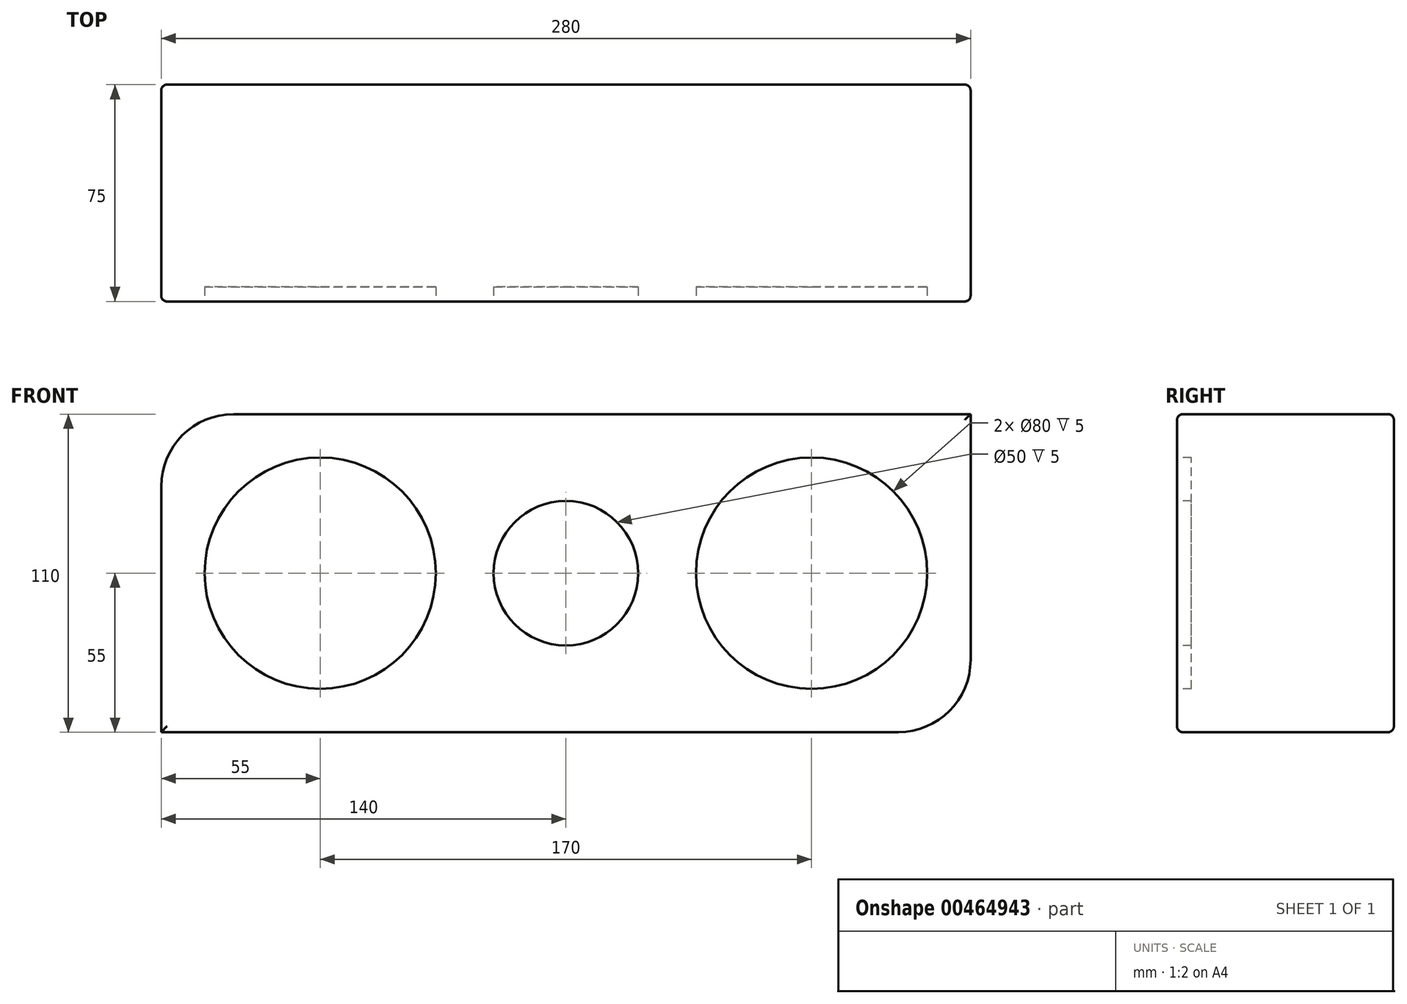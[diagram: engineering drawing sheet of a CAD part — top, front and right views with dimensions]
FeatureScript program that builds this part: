
annotation { "Feature Type Name" : "Feature", "Feature Type Description" : "" }
export const myFeature = defineFeature(function(context is Context, id is Id, definition is map)
    precondition{}
    {
        {
            var Q0;
            Q0=qCreatedBy(makeId("Front.planeOp"),FACE);
            var sketch = newSketch(context, id + "F0", { "sketchPlane" : qUnion([Q0])});
            skLineSegment(sketch, "E0.bottom", {"start": v(-140, -55) * mm, "end": v(115, -55) * mm});
            skLineSegment(sketch, "E0.top", {"start": v(-115, 55) * mm, "end": v(140, 55) * mm});
            skLineSegment(sketch, "E0.left", {"start": v(-140, -55) * mm, "end": v(-140, 30) * mm});
            skLineSegment(sketch, "E0.right", {"start": v(140, -30) * mm, "end": v(140, 55) * mm});
            skPoint(sketch, "E1.visualSharp", {"position": v(-140, 55) * mm});
            skArc(sketch, "E1.filletArc", {"start": v(-115, 55) * mm, "mid": v(-132.68, 47.68) * mm, "end": v(-140, 30) * mm});
            skPoint(sketch, "E2.visualSharp", {"position": v(140, -55) * mm});
            skArc(sketch, "E2.filletArc", {"start": v(115, -55) * mm, "mid": v(132.68, -47.68) * mm, "end": v(140, -30) * mm});
            skSolve(sketch);
        }
        {
            var Q0;
            Q0 = qSketchRegion(id + "F0", true);
            extrude(context, id + "F1", {"entities" : qUnion([Q0]), "depth" : 75 * mm});
        }
        {
            var Q0;
            Q0=makeQuery(id+"F1.opExtrude","CAP_FACE",FACE,{"disambiguationData":[OSD([sQuery(id+"F0.wireOp",EDGE,"E0.bottom"),sQuery(id+"F0.wireOp",EDGE,"E0.top"),sQuery(id+"F0.wireOp",EDGE,"E0.left"),sQuery(id+"F0.wireOp",EDGE,"E0.right"),sQuery(id+"F0.wireOp",EDGE,"E1.filletArc"),sQuery(id+"F0.wireOp",EDGE,"6fe3aa33-5670-4923-973d-67d25d1ae22a.filletArc")])],"isStart":false});
            var Q1;
            Q1=makeQuery(id+"F1.opExtrude","CAP_FACE",FACE,{"disambiguationData":[OSD([sQuery(id+"F0.wireOp",EDGE,"E0.bottom"),sQuery(id+"F0.wireOp",EDGE,"E0.top"),sQuery(id+"F0.wireOp",EDGE,"E0.left"),sQuery(id+"F0.wireOp",EDGE,"E0.right"),sQuery(id+"F0.wireOp",EDGE,"E1.filletArc"),sQuery(id+"F0.wireOp",EDGE,"6fe3aa33-5670-4923-973d-67d25d1ae22a.filletArc")])],"isStart":true});
            fillet(context, id + "F2", {"entities" : qUnion([Q0, Q1]), "radius" : 2 * mm, "tangentPropagation" : true, "allowEdgeOverflow" : false});
        }
        {
            var Q0;
            Q0=makeQuery(id+"F1.opExtrude","CAP_FACE",FACE,{"disambiguationData":[OSD([sQuery(id+"F0.wireOp",EDGE,"E0.bottom"),sQuery(id+"F0.wireOp",EDGE,"E0.top"),sQuery(id+"F0.wireOp",EDGE,"E0.left"),sQuery(id+"F0.wireOp",EDGE,"E0.right"),sQuery(id+"F0.wireOp",EDGE,"E1.filletArc"),sQuery(id+"F0.wireOp",EDGE,"E2.filletArc")])],"isStart":false});
            var sketch = newSketch(context, id + "F3", { "sketchPlane" : qUnion([Q0])});
            skCircle(sketch, "E3", {"center": v(0, 0) * mm, "radius": 25 * mm});
            skCircle(sketch, "E4", {"center": v(-85, 0) * mm, "radius": 40 * mm});
            skCircle(sketch, "E5", {"center": v(85, 0) * mm, "radius": 40 * mm});
            skSolve(sketch);
        }
        {
            var Q0;
            Q0 = qSketchRegion(id + "F3", true);
            extrude(context, id + "F4", {"entities" : qUnion([Q0]), "operationType" : NewBodyOperationType.REMOVE, "oppositeDirection" : true, "depth" : 5 * mm});
        }
    });
